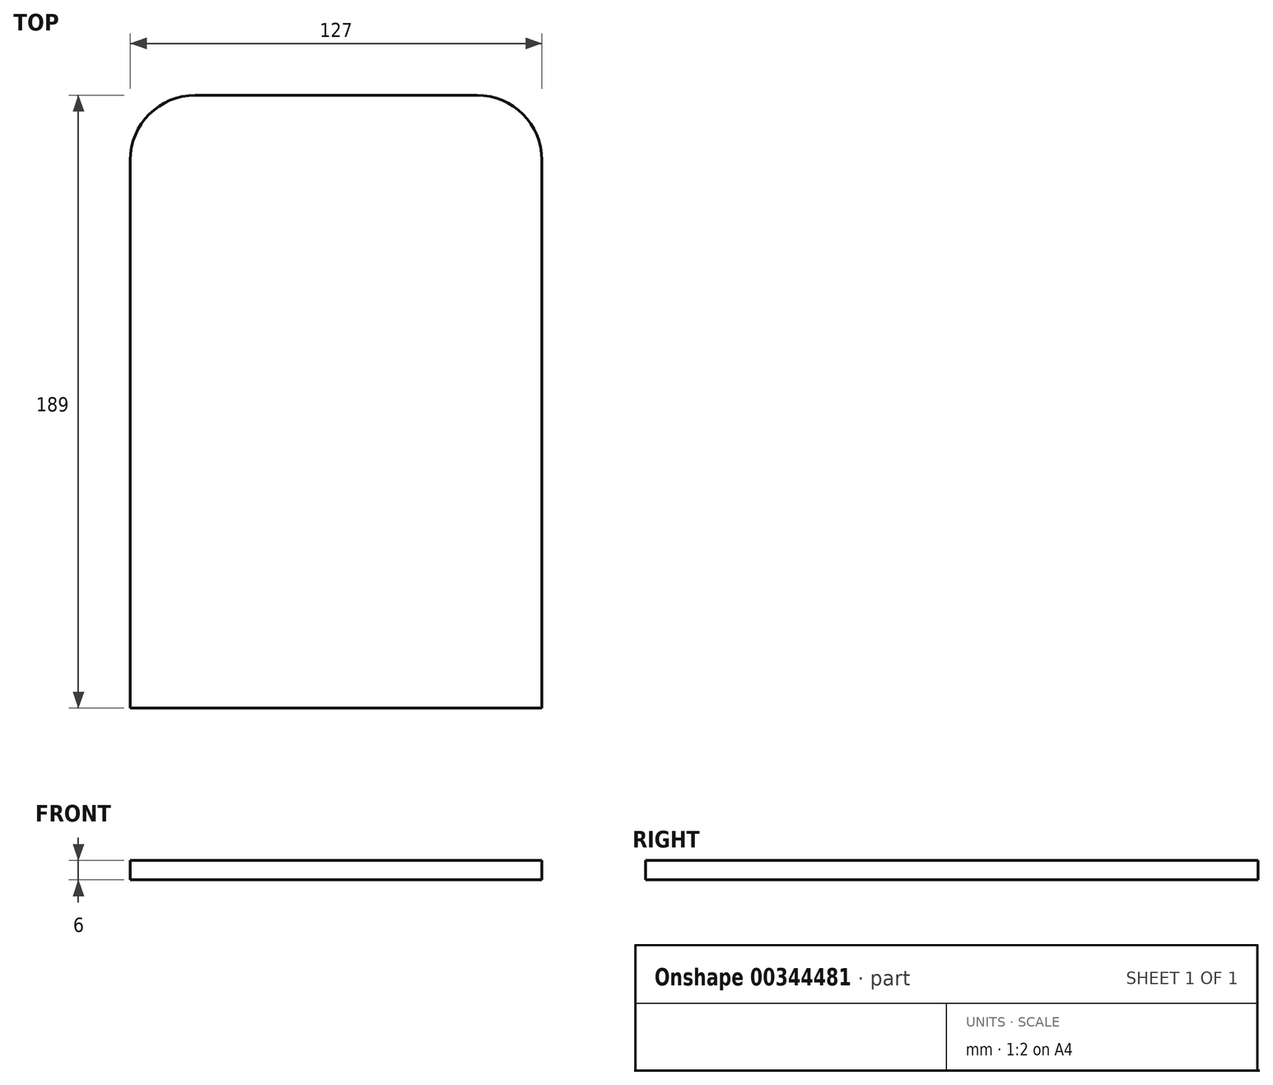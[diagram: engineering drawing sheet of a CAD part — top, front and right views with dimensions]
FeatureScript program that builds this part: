
annotation { "Feature Type Name" : "Feature", "Feature Type Description" : "" }
export const myFeature = defineFeature(function(context is Context, id is Id, definition is map)
    precondition{}
    {
        {
            var Q0;
            Q0=qCreatedBy(makeId("Top.planeOp"),FACE);
            var sketch = newSketch(context, id + "F0", { "sketchPlane" : qUnion([Q0])});
            skLineSegment(sketch, "E0.bottom", {"start": v(0, 0) * mm, "end": v(127, 0) * mm});
            skLineSegment(sketch, "E0.top", {"start": v(20, 189) * mm, "end": v(107, 189) * mm});
            skLineSegment(sketch, "E0.left", {"start": v(0, 0) * mm, "end": v(0, 169) * mm});
            skLineSegment(sketch, "E0.right", {"start": v(127, 0) * mm, "end": v(127, 169) * mm});
            skPoint(sketch, "E1.visualSharp", {"position": v(0, 189) * mm});
            skArc(sketch, "E1.filletArc", {"start": v(20, 189) * mm, "mid": v(5.86, 183.14) * mm, "end": v(0, 169) * mm});
            skPoint(sketch, "E2.visualSharp", {"position": v(127, 189) * mm});
            skArc(sketch, "E2.filletArc", {"start": v(127, 169) * mm, "mid": v(121.14, 183.14) * mm, "end": v(107, 189) * mm});
            skSolve(sketch);
        }
        {
            var Q0;
            Q0 = qSketchRegion(id + "F0", true);
            extrude(context, id + "F1", {"entities" : qUnion([Q0]), "depth" : 6 * mm, "offsetDistance" : 25 * mm});
        }
    });
